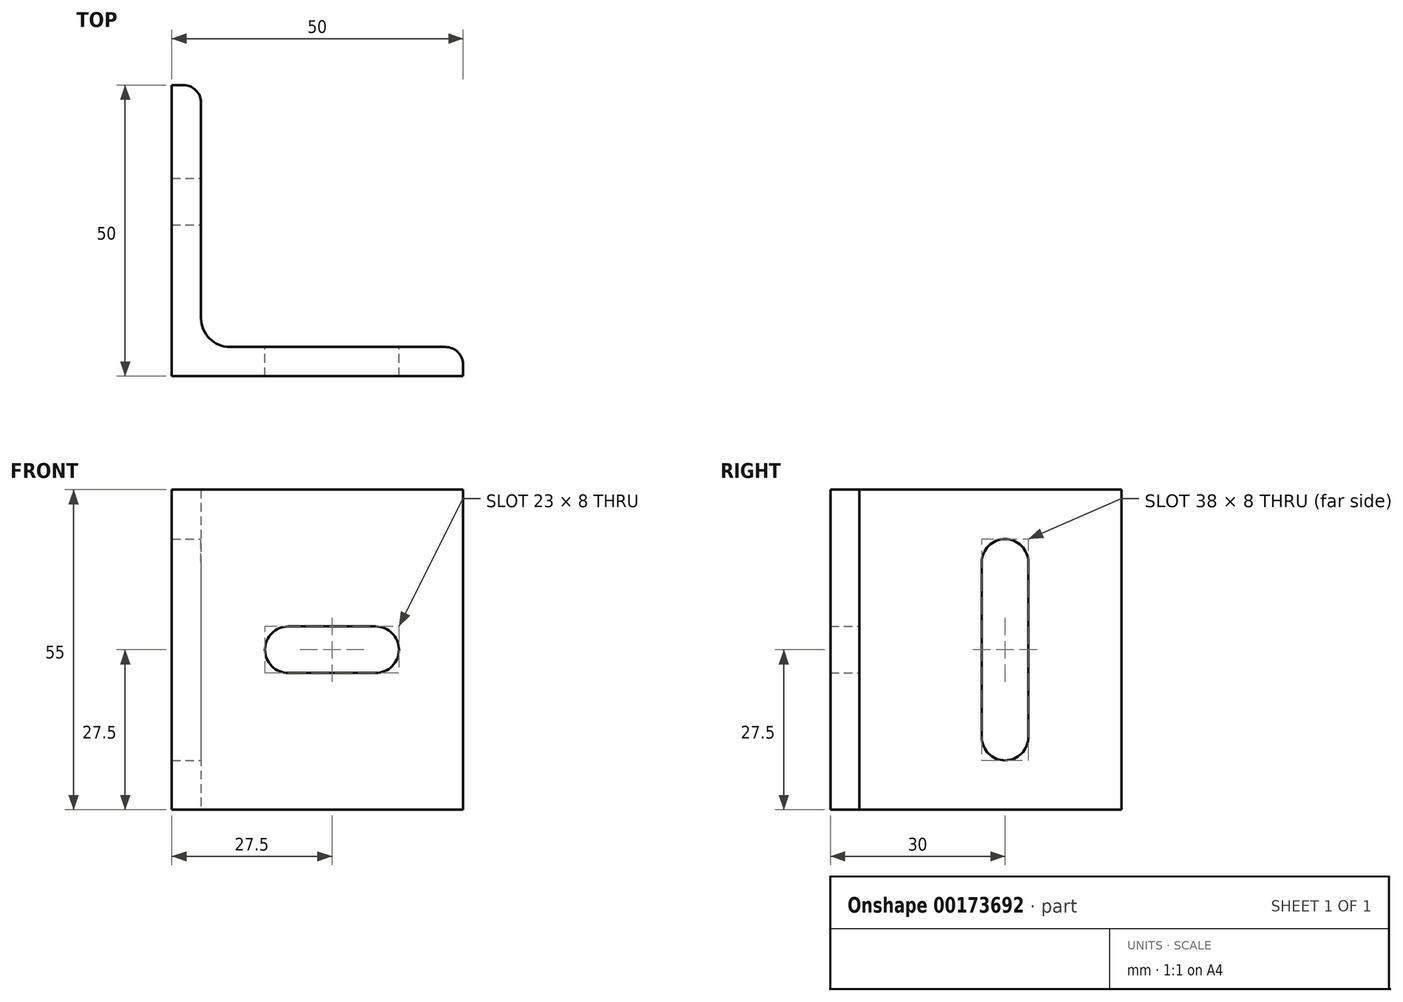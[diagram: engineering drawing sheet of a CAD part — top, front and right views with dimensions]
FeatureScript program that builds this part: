
annotation { "Feature Type Name" : "Feature", "Feature Type Description" : "" }
export const myFeature = defineFeature(function(context is Context, id is Id, definition is map)
    precondition{}
    {
        {
            var Q0;
            Q0=qCreatedBy(makeId("Top.planeOp"),FACE);
            var sketch = newSketch(context, id + "F0", { "sketchPlane" : qUnion([Q0])});
            skLineSegment(sketch, "E0", {"start": v(0, 0) * mm, "end": v(0, -50) * mm});
            skLineSegment(sketch, "E1", {"start": v(0, -50) * mm, "end": v(50, -50) * mm});
            skLineSegment(sketch, "E2.0", {"start": v(5, -45) * mm, "end": v(50, -45) * mm});
            skLineSegment(sketch, "E2.1", {"start": v(5, 0) * mm, "end": v(5, -45) * mm});
            skLineSegment(sketch, "E3", {"start": v(5, 0) * mm, "end": v(0, 0) * mm});
            skLineSegment(sketch, "E4", {"start": v(50, -50) * mm, "end": v(50, -45) * mm});
            skSolve(sketch);
        }
        {
            var Q0;
            Q0=qSketchRegion(id+"F0",true);
            extrude(context, id + "F1", {"entities" : qUnion([Q0]), "endBound" : BoundingType.SYMMETRIC, "depth" : 55 * mm});
        }
        {
            var Q0;
            Q0=makeQuery(id+"F1.opExtrude","SWEPT_EDGE",EDGE,{"disambiguationData":[OSD([sQuery(id+"F0.wireOp",EDGE,"E2.0"),sQuery(id+"F0.wireOp",EDGE,"E2.1")])]});
            fillet(context, id + "F2", {"entities" : qUnion([Q0]), "radius" : 5 * mm, "tangentPropagation" : true, "allowEdgeOverflow" : false});
        }
        {
            var Q0;
            Q0=makeQuery(id+"F1.opExtrude","SWEPT_EDGE",EDGE,{"disambiguationData":[OSD([sQuery(id+"F0.wireOp",EDGE,"E2.1"),sQuery(id+"F0.wireOp",EDGE,"E3")])]});
            var Q1;
            Q1=makeQuery(id+"F1.opExtrude","SWEPT_EDGE",EDGE,{"disambiguationData":[OSD([sQuery(id+"F0.wireOp",EDGE,"E2.0"),sQuery(id+"F0.wireOp",EDGE,"E4")])]});
            fillet(context, id + "F3", {"entities" : qUnion([Q0, Q1]), "radius" : 3 * mm, "tangentPropagation" : true, "allowEdgeOverflow" : false});
        }
        {
            var Q0;
            Q0=makeQuery(id+"F1.opExtrude","SWEPT_FACE",FACE,{"disambiguationData":[OSD([sQuery(id+"F0.wireOp",EDGE,"E2.1")])]});
            var sketch = newSketch(context, id + "F4", { "sketchPlane" : qUnion([Q0])});
            skLineSegment(sketch, "E5.bottom", {"start": v(-24, 15) * mm, "end": v(-16, 15) * mm, "construction": true});
            skLineSegment(sketch, "E5.top", {"start": v(-24, -15) * mm, "end": v(-16, -15) * mm, "construction": true});
            skLineSegment(sketch, "E5.left", {"start": v(-24, 15) * mm, "end": v(-24, -15) * mm});
            skLineSegment(sketch, "E5.right", {"start": v(-16, 15) * mm, "end": v(-16, -15) * mm});
            skLineSegment(sketch, "E6", {"start": v(0, 0) * mm, "end": v(-16, 0) * mm, "construction": true});
            skArc(sketch, "E7", {"start": v(-16, 15) * mm, "mid": v(-20, 19) * mm, "end": v(-24, 15) * mm});
            skArc(sketch, "E8", {"start": v(-24, -15) * mm, "mid": v(-20, -19) * mm, "end": v(-16, -15) * mm});
            skSolve(sketch);
        }
        {
            var Q0;
            Q0=qSketchRegion(id+"F4",true);
            extrude(context, id + "F5", {"entities" : qUnion([Q0]), "operationType" : NewBodyOperationType.REMOVE, "endBound" : BoundingType.THROUGH_ALL, "oppositeDirection" : true, "depth" : 25 * mm});
        }
        {
            var Q0;
            Q0=makeQuery(id+"F1.opExtrude","SWEPT_FACE",FACE,{"disambiguationData":[OSD([sQuery(id+"F0.wireOp",EDGE,"E2.0")])]});
            var sketch = newSketch(context, id + "F6", { "sketchPlane" : qUnion([Q0])});
            skLineSegment(sketch, "E9.bottom", {"start": v(-35, 4) * mm, "end": v(-20, 4) * mm});
            skLineSegment(sketch, "E9.top", {"start": v(-35, -4) * mm, "end": v(-20, -4) * mm});
            skLineSegment(sketch, "E9.left", {"start": v(-35, 4) * mm, "end": v(-35, -4) * mm, "construction": true});
            skLineSegment(sketch, "E9.right", {"start": v(-20, 4) * mm, "end": v(-20, -4) * mm, "construction": true});
            skLineSegment(sketch, "E10", {"start": v(0, 0) * mm, "end": v(-20, 0) * mm, "construction": true});
            skArc(sketch, "E11", {"start": v(-35, 4) * mm, "mid": v(-39, 0) * mm, "end": v(-35, -4) * mm});
            skArc(sketch, "E12", {"start": v(-20, -4) * mm, "mid": v(-16, 0) * mm, "end": v(-20, 4) * mm});
            skSolve(sketch);
        }
        {
            var Q0;
            Q0=qSketchRegion(id+"F6",true);
            extrude(context, id + "F7", {"entities" : qUnion([Q0]), "operationType" : NewBodyOperationType.REMOVE, "endBound" : BoundingType.THROUGH_ALL, "oppositeDirection" : true, "depth" : 25 * mm});
        }
    });
